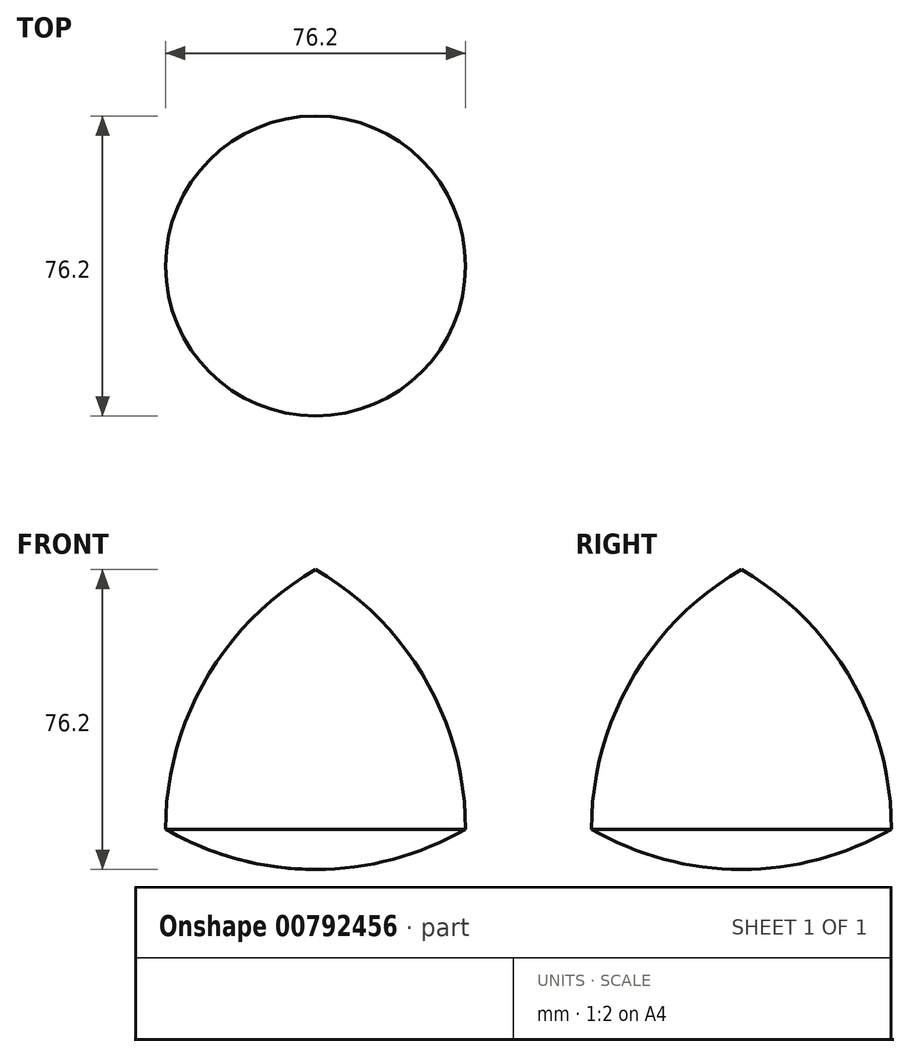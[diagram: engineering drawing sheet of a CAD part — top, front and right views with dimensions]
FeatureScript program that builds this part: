
annotation { "Feature Type Name" : "Feature", "Feature Type Description" : "" }
export const myFeature = defineFeature(function(context is Context, id is Id, definition is map)
    precondition{}
    {
        {
            var Q0;
            Q0=qCreatedBy(makeId("Front.planeOp"), FACE);
            var sketch = newSketch(context, id + "F0", { "sketchPlane" : qUnion([Q0])});
            skLineSegment(sketch, "E0", {"start": v(-38.1, 0) * mm, "end": v(38.1, 0) * mm});
            skLineSegment(sketch, "E1", {"start": v(38.1, 0) * mm, "end": v(0, 66) * mm});
            skLineSegment(sketch, "E2", {"start": v(0, 66) * mm, "end": v(-38.1, 0) * mm});
            skArc(sketch, "E3", {"start": v(38.1, 0) * mm, "mid": v(27.9, 38.1) * mm, "end": v(0, 66) * mm});
            skArc(sketch, "E4", {"start": v(0, 66) * mm, "mid": v(-27.9, 38.1) * mm, "end": v(-38.1, 0) * mm});
            skArc(sketch, "E5", {"start": v(-38.1, 0) * mm, "mid": v(0, -10.2) * mm, "end": v(38.1, 0) * mm});
            skLineSegment(sketch, "E6", {"start": v(0, 66) * mm, "end": v(0, -10.2) * mm});
            skPoint(sketch, "E7", {"position": v(27.9, 38.1) * mm});
            skPoint(sketch, "E8", {"position": v(-27.9, 38.1) * mm});
            skPoint(sketch, "E9", {"position": v(0, -10.2) * mm});
            skSolve(sketch);
        }
        {
            var Q0;
            Q0=makeQuery(id+"F0.imprint","IMPRINT",FACE,{"disambiguationData":[TD([[makeQuery(id+"F0.imprint","IMPRINT",EDGE,{"derivedFrom":sQuery(id+"F0.wireOp",EDGE,"E2")}),-1.0]])]});
            var Q1;
            {var subQ1=sQuery(id+"F0.wireOp",EDGE,"E2");Q1=makeQuery(id+"F0.imprint","IMPRINT",FACE,{"disambiguationData":[TD([[makeQuery(id+"F0.imprint","IMPRINT",EDGE,{"derivedFrom":subQ1}),1.0]])]});}
            var Q2;
            {var subQ0=sQuery(id+"F0.wireOp",EDGE,"E5");var subQ3=sQuery(id+"F0.wireOp",EDGE,"E6");var subQ5=makeQuery(id+"F0.imprint","INTERSECT",VERTEX,{"derivedFrom":[subQ0,subQ3]});Q2=makeQuery(id+"F0.imprint","IMPRINT",FACE,{"disambiguationData":[TD([[makeQuery(id+"F0.imprint","IMPRINT",EDGE,{"disambiguationData":[TD([[subQ5,1.0]])],"derivedFrom":subQ3}),-1.0]])]});}
            var Q3;
            Q3=sQuery(id+"F0.wireOp",EDGE,"E6");
            revolve(context, id + "F1", {"surfaceOperationType" : NewSurfaceOperationType.NEW, "entities" : qUnion([Q0, Q1, Q2]), "axis" : qUnion([Q3]), "revolveType" : RevolveType.FULL});
        }
    });
